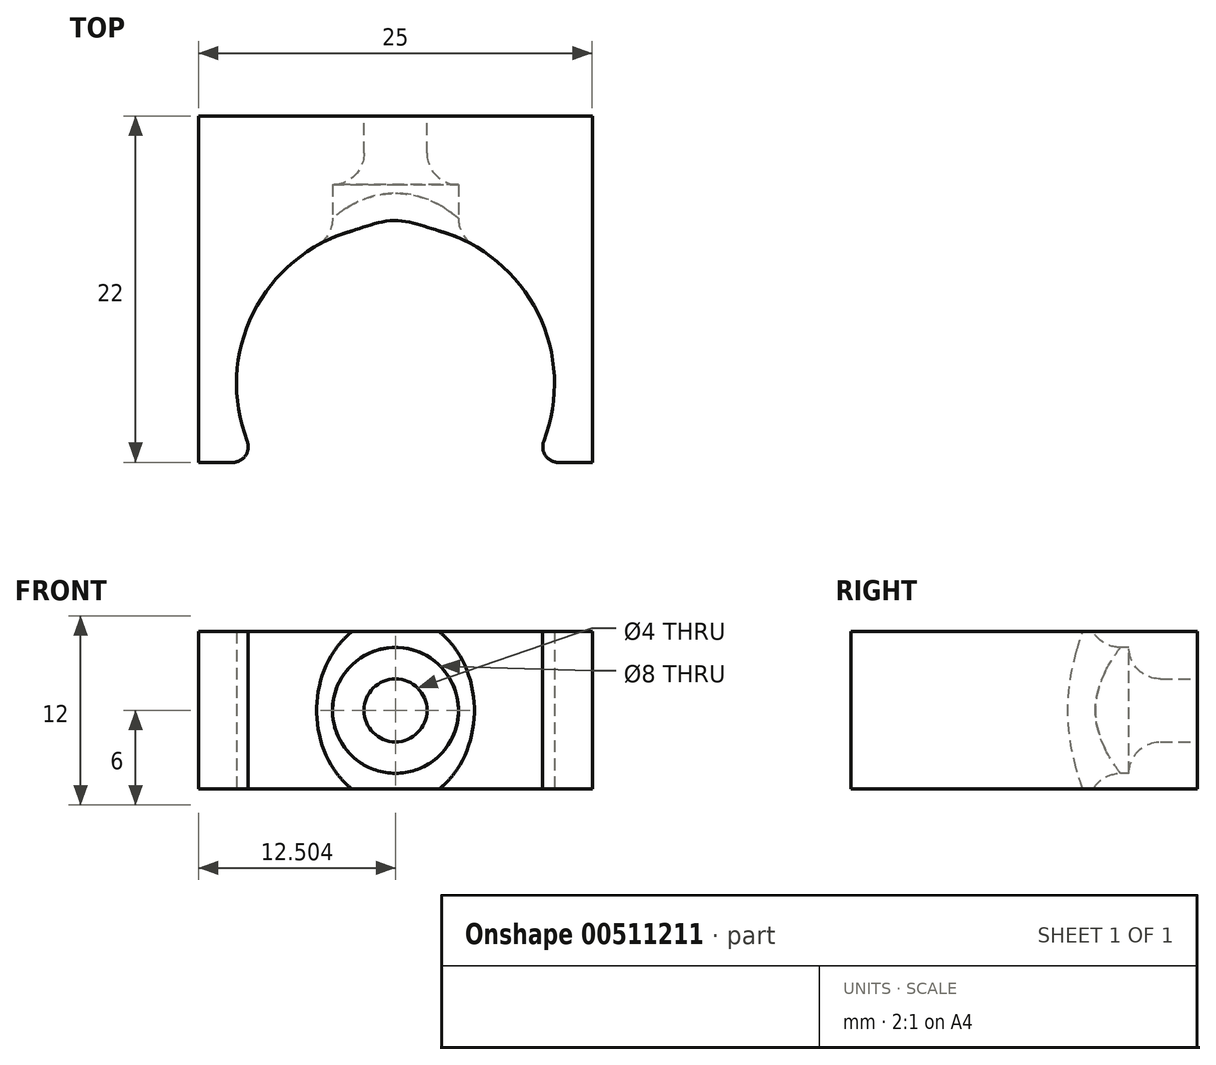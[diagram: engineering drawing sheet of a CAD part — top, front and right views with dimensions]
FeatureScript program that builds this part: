
annotation { "Feature Type Name" : "Feature", "Feature Type Description" : "" }
export const myFeature = defineFeature(function(context is Context, id is Id, definition is map)
    precondition{}
    {
        {
            var Q0;
            Q0=qCreatedBy(makeId("Top.planeOp"),FACE);
            var sketch = newSketch(context, id + "F0", { "sketchPlane" : qUnion([Q0])});
            skLineSegment(sketch, "E0.bottom", {"start": v(10.32, -10.64) * mm, "end": v(35.32, -10.64) * mm});
            skLineSegment(sketch, "E0.top", {"start": v(10.32, -32.64) * mm, "end": v(35.32, -32.64) * mm});
            skLineSegment(sketch, "E0.left", {"start": v(10.32, -10.64) * mm, "end": v(10.32, -32.64) * mm});
            skLineSegment(sketch, "E0.right", {"start": v(35.32, -10.64) * mm, "end": v(35.32, -32.64) * mm});
            skCircle(sketch, "E1", {"center": v(22.82, -27.64) * mm, "radius": 10.1 * mm});
            skSolve(sketch);
        }
        {
            var Q0;
            Q0=makeQuery(id+"F0.imprint","IMPRINT",FACE,{"disambiguationData":[TD([[makeQuery(id+"F0.imprint","IMPRINT",EDGE,{"derivedFrom":sQuery(id+"F0.wireOp",EDGE,"E0.bottom")}),-1.0]])]});
            extrude(context, id + "F1", {"entities" : qUnion([Q0]), "depth" : 10 * mm});
        }
        {
            var Q0;
            Q0=makeQuery(id+"F1.opExtrude","SWEPT_FACE",FACE,{"disambiguationData":[OSD([sQuery(id+"F0.wireOp",EDGE,"E0.bottom")])]});
            var sketch = newSketch(context, id + "F2", { "sketchPlane" : qUnion([Q0])});
            skCircle(sketch, "E2", {"center": v(-22.82, 5) * mm, "radius": 2 * mm});
            skCircle(sketch, "E3", {"center": v(-22.82, 5) * mm, "radius": 4 * mm});
            skSolve(sketch);
        }
        {
            var Q0;
            Q0=makeQuery(id+"F2.imprint","IMPRINT",FACE,{"disambiguationData":[TD([[makeQuery(id+"F2.imprint","IMPRINT",EDGE,{"derivedFrom":sQuery(id+"F2.wireOp",EDGE,"E2")}),1.0]])]});
            extrude(context, id + "F3", {"entities" : qUnion([Q0]), "operationType" : NewBodyOperationType.REMOVE, "endBound" : BoundingType.UP_TO_NEXT, "oppositeDirection" : true, "depth" : 25 * mm});
        }
        {
            var Q0;
            {var subQ0=sQuery(id+"F0.wireOp",EDGE,"E1");var subQ1=sQuery(id+"F0.wireOp",EDGE,"E0.top");Q0=makeQuery(id+"F1.opExtrude","SWEPT_EDGE",EDGE,{"disambiguationData":[OSD([subQ1,subQ0]),TDD([makeQuery(id+"F0.imprint","INTERSECT",VERTEX,{"disambiguationData":[OD(0.0)],"derivedFrom":[subQ1,subQ0]})])]});}
            var Q1;
            {var subQ0=sQuery(id+"F0.wireOp",EDGE,"E1");var subQ1=sQuery(id+"F0.wireOp",EDGE,"E0.top");Q1=makeQuery(id+"F1.opExtrude","SWEPT_EDGE",EDGE,{"disambiguationData":[OSD([subQ1,subQ0]),TDD([makeQuery(id+"F0.imprint","INTERSECT",VERTEX,{"disambiguationData":[OD(1.0)],"derivedFrom":[subQ1,subQ0]})])]});}
            fillet(context, id + "F4", {"entities" : qUnion([Q0, Q1]), "radius" : 1 * mm, "tangentPropagation" : true, "allowEdgeOverflow" : false});
        }
        {
            var Q0;
            Q0=qCreatedBy(makeId("Front.planeOp"),FACE);
            cPlane(context, id + "F5", {"entities" : qUnion([Q0]), "cplaneType" : CPlaneType.OFFSET, "offset" : 18 * mm, "width" : 150 * mm, "height" : 150 * mm});
        }
        {
            var Q0;
            Q0=qCreatedBy(id+"F5.planeOp",FACE);
            var sketch = newSketch(context, id + "F6", { "sketchPlane" : qUnion([Q0])});
            skCircle(sketch, "E4.0", {"center": v(22.82, 5) * mm, "radius": 4 * mm});
            skCircle(sketch, "E5.0", {"center": v(22.82, 5) * mm, "radius": 2 * mm});
            skSolve(sketch);
        }
        {
            var Q0;
            Q0=makeQuery(id+"F6.imprint","IMPRINT",FACE,{"disambiguationData":[TD([[makeQuery(id+"F6.imprint","IMPRINT",EDGE,{"derivedFrom":sQuery(id+"F6.wireOp",EDGE,"E4.0")}),-1.0]])]});
            var Q1;
            Q1=makeQuery(id+"F6.imprint","IMPRINT",FACE,{"disambiguationData":[TD([[makeQuery(id+"F6.imprint","IMPRINT",EDGE,{"derivedFrom":sQuery(id+"F6.wireOp",EDGE,"E5.0")}),-1.0]])]});
            extrude(context, id + "F7", {"entities" : qUnion([Q0, Q1]), "operationType" : NewBodyOperationType.REMOVE, "oppositeDirection" : true, "depth" : 3 * mm});
        }
        {
            var Q0;
            Q0=makeQuery(id+"F7.boolean.opBoolean","INTERSECT",EDGE,{"disambiguationData":[OD(1.0)],"derivedFrom":[makeQuery(id+"F1.opExtrude","SWEPT_FACE",FACE,{"disambiguationData":[OSD([sQuery(id+"F0.wireOp",EDGE,"E1")])]}),makeQuery(id+"F7.opExtrude","SWEPT_FACE",FACE,{"disambiguationData":[OSD([sQuery(id+"F6.wireOp",EDGE,"E4.0")])]})]});
            var Q1;
            Q1=makeQuery(id+"F7.boolean.opBoolean","INTERSECT",EDGE,{"disambiguationData":[OD(0.0)],"derivedFrom":[makeQuery(id+"F1.opExtrude","SWEPT_FACE",FACE,{"disambiguationData":[OSD([sQuery(id+"F0.wireOp",EDGE,"E1")])]}),makeQuery(id+"F7.opExtrude","CAP_FACE",FACE,{"disambiguationData":[OSD([sQuery(id+"F6.wireOp",EDGE,"E4.0")])],"isStart":true})]});
            var Q2;
            Q2=makeQuery(id+"F7.boolean.opBoolean","INTERSECT",EDGE,{"disambiguationData":[OD(0.0)],"derivedFrom":[makeQuery(id+"F1.opExtrude","SWEPT_FACE",FACE,{"disambiguationData":[OSD([sQuery(id+"F0.wireOp",EDGE,"E1")])]}),makeQuery(id+"F7.opExtrude","SWEPT_FACE",FACE,{"disambiguationData":[OSD([sQuery(id+"F6.wireOp",EDGE,"E4.0")])]})]});
            var Q3;
            Q3=makeQuery(id+"F7.boolean.opBoolean","INTERSECT",EDGE,{"disambiguationData":[OD(1.0)],"derivedFrom":[makeQuery(id+"F1.opExtrude","SWEPT_FACE",FACE,{"disambiguationData":[OSD([sQuery(id+"F0.wireOp",EDGE,"E1")])]}),makeQuery(id+"F7.opExtrude","CAP_FACE",FACE,{"disambiguationData":[OSD([sQuery(id+"F6.wireOp",EDGE,"E4.0")])],"isStart":true})]});
            var Q4;
            Q4=makeQuery(id+"F7.boolean.opBoolean","INTERSECT",EDGE,{"derivedFrom":[makeQuery(id+"F3.boolean.opBoolean","COPY",FACE,{"derivedFrom":makeQuery(id+"F3.opExtrude","SWEPT_FACE",FACE,{"disambiguationData":[OSD([sQuery(id+"F2.wireOp",EDGE,"E2")])]})}),makeQuery(id+"F7.opExtrude","CAP_FACE",FACE,{"disambiguationData":[OSD([sQuery(id+"F6.wireOp",EDGE,"E4.0")])],"isStart":false})]});
            fillet(context, id + "F8", {"entities" : qUnion([Q0, Q1, Q2, Q3, Q4]), "radius" : 2 * mm, "tangentPropagation" : true, "allowEdgeOverflow" : false});
        }
    });
